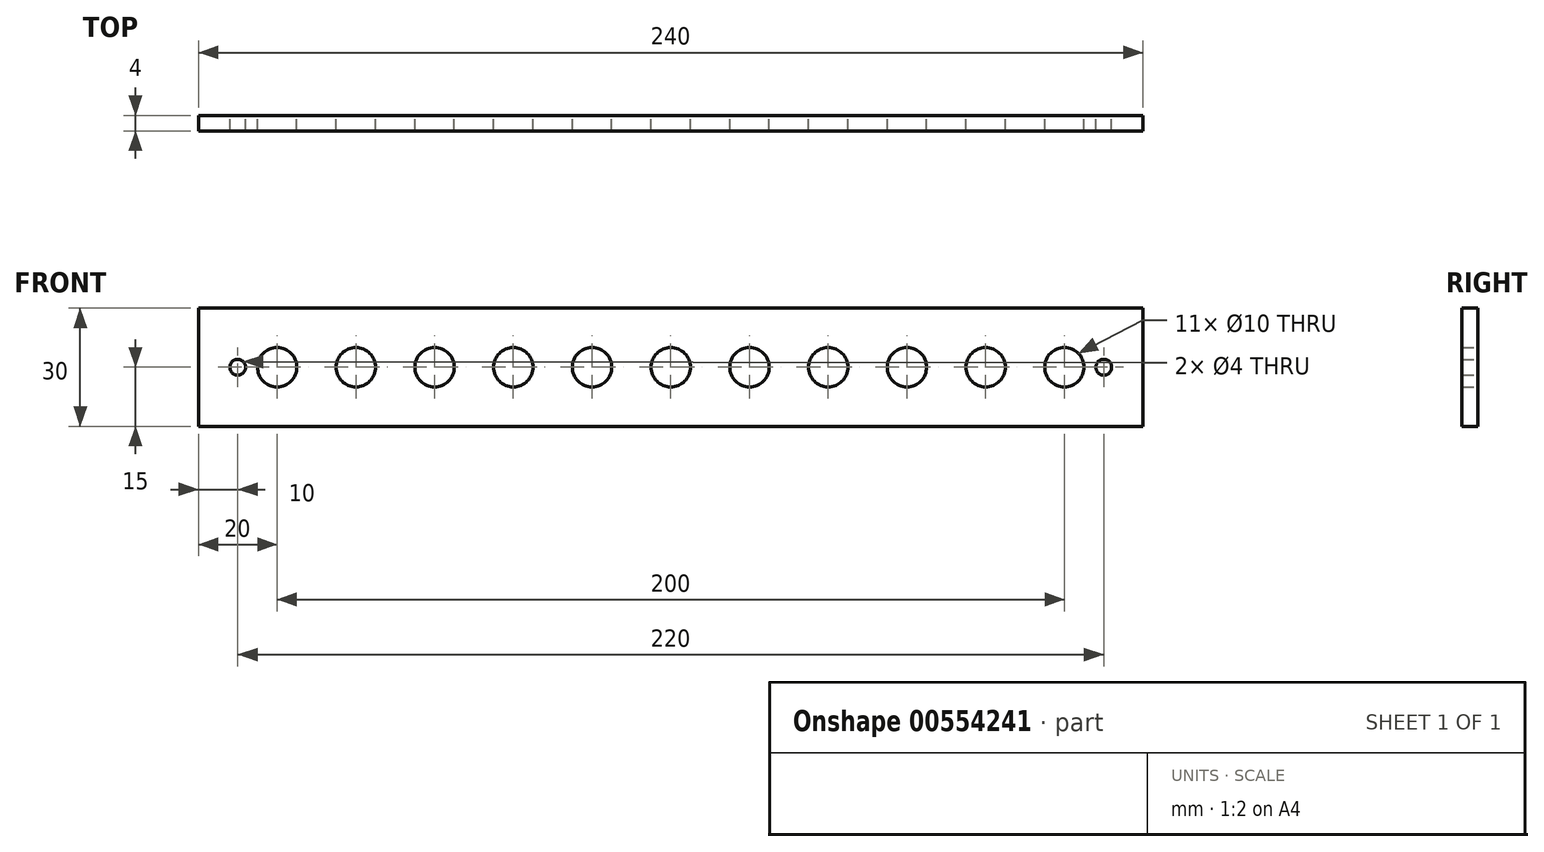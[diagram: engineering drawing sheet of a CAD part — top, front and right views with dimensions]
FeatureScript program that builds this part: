
annotation { "Feature Type Name" : "Feature", "Feature Type Description" : "" }
export const myFeature = defineFeature(function(context is Context, id is Id, definition is map)
    precondition{}
    {
        {
            var Q0;
            Q0=qCreatedBy(makeId("Front.planeOp"),FACE);
            var sketch = newSketch(context, id + "F0", { "sketchPlane" : qUnion([Q0])});
            skLineSegment(sketch, "E0.bottom", {"start": v(120, -15) * mm, "end": v(-120, -15) * mm});
            skLineSegment(sketch, "E0.top", {"start": v(120, 15) * mm, "end": v(-120, 15) * mm});
            skLineSegment(sketch, "E0.left", {"start": v(120, -15) * mm, "end": v(120, 15) * mm});
            skLineSegment(sketch, "E0.right", {"start": v(-120, -15) * mm, "end": v(-120, 15) * mm});
            skPoint(sketch, "E0.middle", {"position": v(0, 0) * mm});
            skLineSegment(sketch, "E1.bottom", {"start": v(100, -5) * mm, "end": v(-100, -5) * mm});
            skLineSegment(sketch, "E1.top", {"start": v(100, 5) * mm, "end": v(-100, 5) * mm});
            skLineSegment(sketch, "E1.left", {"start": v(100, -5) * mm, "end": v(100, 5) * mm});
            skLineSegment(sketch, "E1.right", {"start": v(-100, -5) * mm, "end": v(-100, 5) * mm});
            skPoint(sketch, "E2.startSnap0", {"position": v(120, 0) * mm});
            skPoint(sketch, "E2.endSnap0", {"position": v(100, 0) * mm});
            skCircle(sketch, "E3", {"center": v(-100, 0) * mm, "radius": 5 * mm});
            skCircle(sketch, "E4", {"center": v(-80, 0) * mm, "radius": 5 * mm});
            skCircle(sketch, "E5", {"center": v(-60, 0) * mm, "radius": 5 * mm});
            skCircle(sketch, "E6", {"center": v(-40, 0) * mm, "radius": 5 * mm});
            skCircle(sketch, "E7", {"center": v(40, 0) * mm, "radius": 5 * mm});
            skCircle(sketch, "E8", {"center": v(60, 0) * mm, "radius": 5 * mm});
            skCircle(sketch, "E9", {"center": v(80, 0) * mm, "radius": 5 * mm});
            skCircle(sketch, "E10", {"center": v(100, 0) * mm, "radius": 5 * mm});
            skCircle(sketch, "E11", {"center": v(-20, 0) * mm, "radius": 5 * mm});
            skCircle(sketch, "E12", {"center": v(0, 0) * mm, "radius": 5 * mm});
            skCircle(sketch, "E13", {"center": v(20, 0) * mm, "radius": 5 * mm});
            skCircle(sketch, "E14", {"center": v(110, 0) * mm, "radius": 2 * mm});
            skCircle(sketch, "E15", {"center": v(-110, 0) * mm, "radius": 2 * mm});
            skSolve(sketch);
        }
        {
            var Q0;
            Q0=makeQuery(id+"F0.imprint","IMPRINT",FACE,{"disambiguationData":[TD([[makeQuery(id+"F0.imprint","IMPRINT",EDGE,{"derivedFrom":sQuery(id+"F0.wireOp",EDGE,"E0.bottom")}),-1.0]])]});
            var Q1;
            {var subQ2=sQuery(id+"F0.wireOp",EDGE,"E1.bottom");var subQ4=sQuery(id+"F0.wireOp",EDGE,"E4");var subQ5=makeQuery(id+"F0.imprint","INTERSECT",VERTEX,{"derivedFrom":[subQ2,subQ4]});Q1=makeQuery(id+"F0.imprint","IMPRINT",FACE,{"disambiguationData":[TD([[makeQuery(id+"F0.imprint","IMPRINT",EDGE,{"disambiguationData":[TD([[subQ5,1.0]])],"derivedFrom":subQ4}),-1.0]])]});}
            var Q2;
            {var subQ0=sQuery(id+"F0.wireOp",EDGE,"E5");var subQ1=sQuery(id+"F0.wireOp",EDGE,"E1.bottom");var subQ2=makeQuery(id+"F0.imprint","INTERSECT",VERTEX,{"derivedFrom":[subQ1,subQ0]});Q2=makeQuery(id+"F0.imprint","IMPRINT",FACE,{"disambiguationData":[TD([[makeQuery(id+"F0.imprint","IMPRINT",EDGE,{"disambiguationData":[TD([[subQ2,-1.0]])],"derivedFrom":subQ1}),-1.0]])]});}
            var Q3;
            {var subQ0=sQuery(id+"F0.wireOp",EDGE,"E6");var subQ1=sQuery(id+"F0.wireOp",EDGE,"E1.bottom");var subQ2=makeQuery(id+"F0.imprint","INTERSECT",VERTEX,{"derivedFrom":[subQ1,subQ0]});Q3=makeQuery(id+"F0.imprint","IMPRINT",FACE,{"disambiguationData":[TD([[makeQuery(id+"F0.imprint","IMPRINT",EDGE,{"disambiguationData":[TD([[subQ2,-1.0]])],"derivedFrom":subQ1}),-1.0]])]});}
            var Q4;
            {var subQ0=sQuery(id+"F0.wireOp",EDGE,"E11");var subQ1=sQuery(id+"F0.wireOp",EDGE,"E1.bottom");var subQ2=makeQuery(id+"F0.imprint","INTERSECT",VERTEX,{"derivedFrom":[subQ1,subQ0]});Q4=makeQuery(id+"F0.imprint","IMPRINT",FACE,{"disambiguationData":[TD([[makeQuery(id+"F0.imprint","IMPRINT",EDGE,{"disambiguationData":[TD([[subQ2,-1.0]])],"derivedFrom":subQ1}),-1.0]])]});}
            var Q5;
            {var subQ0=sQuery(id+"F0.wireOp",EDGE,"E12");var subQ1=sQuery(id+"F0.wireOp",EDGE,"E1.bottom");var subQ2=makeQuery(id+"F0.imprint","INTERSECT",VERTEX,{"derivedFrom":[subQ1,subQ0]});Q5=makeQuery(id+"F0.imprint","IMPRINT",FACE,{"disambiguationData":[TD([[makeQuery(id+"F0.imprint","IMPRINT",EDGE,{"disambiguationData":[TD([[subQ2,-1.0]])],"derivedFrom":subQ1}),-1.0]])]});}
            var Q6;
            {var subQ0=sQuery(id+"F0.wireOp",EDGE,"E13");var subQ1=sQuery(id+"F0.wireOp",EDGE,"E1.bottom");var subQ2=makeQuery(id+"F0.imprint","INTERSECT",VERTEX,{"derivedFrom":[subQ1,subQ0]});Q6=makeQuery(id+"F0.imprint","IMPRINT",FACE,{"disambiguationData":[TD([[makeQuery(id+"F0.imprint","IMPRINT",EDGE,{"disambiguationData":[TD([[subQ2,-1.0]])],"derivedFrom":subQ1}),-1.0]])]});}
            var Q7;
            {var subQ0=sQuery(id+"F0.wireOp",EDGE,"E7");var subQ1=sQuery(id+"F0.wireOp",EDGE,"E1.bottom");var subQ2=makeQuery(id+"F0.imprint","INTERSECT",VERTEX,{"derivedFrom":[subQ1,subQ0]});Q7=makeQuery(id+"F0.imprint","IMPRINT",FACE,{"disambiguationData":[TD([[makeQuery(id+"F0.imprint","IMPRINT",EDGE,{"disambiguationData":[TD([[subQ2,-1.0]])],"derivedFrom":subQ1}),-1.0]])]});}
            var Q8;
            {var subQ0=sQuery(id+"F0.wireOp",EDGE,"E8");var subQ1=sQuery(id+"F0.wireOp",EDGE,"E1.bottom");var subQ2=makeQuery(id+"F0.imprint","INTERSECT",VERTEX,{"derivedFrom":[subQ1,subQ0]});Q8=makeQuery(id+"F0.imprint","IMPRINT",FACE,{"disambiguationData":[TD([[makeQuery(id+"F0.imprint","IMPRINT",EDGE,{"disambiguationData":[TD([[subQ2,-1.0]])],"derivedFrom":subQ1}),-1.0]])]});}
            var Q9;
            {var subQ0=sQuery(id+"F0.wireOp",EDGE,"E9");var subQ1=sQuery(id+"F0.wireOp",EDGE,"E1.bottom");var subQ2=makeQuery(id+"F0.imprint","INTERSECT",VERTEX,{"derivedFrom":[subQ1,subQ0]});Q9=makeQuery(id+"F0.imprint","IMPRINT",FACE,{"disambiguationData":[TD([[makeQuery(id+"F0.imprint","IMPRINT",EDGE,{"disambiguationData":[TD([[subQ2,-1.0]])],"derivedFrom":subQ1}),-1.0]])]});}
            var Q10;
            {var subQ2=sQuery(id+"F0.wireOp",EDGE,"E1.bottom");var subQ4=sQuery(id+"F0.wireOp",EDGE,"E9");var subQ5=makeQuery(id+"F0.imprint","INTERSECT",VERTEX,{"derivedFrom":[subQ2,subQ4]});Q10=makeQuery(id+"F0.imprint","IMPRINT",FACE,{"disambiguationData":[TD([[makeQuery(id+"F0.imprint","IMPRINT",EDGE,{"disambiguationData":[TD([[subQ5,-1.0]])],"derivedFrom":subQ4}),-1.0]])]});}
            extrude(context, id + "F1", {"entities" : qUnion([Q0, Q1, Q2, Q3, Q4, Q5, Q6, Q7, Q8, Q9, Q10]), "depth" : 4 * mm, "offsetDistance" : 25 * mm});
        }
    });
